# Revit family: T-604_Ciclon CC
name_source: partatom
category: Plumbing Fixtures
revit_build: Autodesk Revit 2015 (Build: 20140606_1530(x64)
units: mm (PartAtom-declared; Revit-internal decimal feet)

## types (3) — shared parameters
Altura máx. de bombeo = 6 m vertical
Amax = 200 mm  [stored 0.656168 ft]
Amin = 75 mm
Anchura = 500 mm  [stored 1.64042 ft]
Bastidor_Material principal = Jimten_Bastidor Azul
Bastidor_Material secundario = Jimten_Bastidor Acero
Carga aparente = 200 VA
Caudal = 1.7 L/s
Certificados = http://www.jimten.com
"
Cisterna = Jimten_Cisterna
Clasificación de cargas = Aparato eléctrico - Unidad de vivienda
Description = CISTERNA EMPOTRADA CON TRITURADOR SANITARIO PARA CUARTO DE BAÑO
Diámetro Cisterna = 40 mm  [stored 0.131234 ft]
Diámetro Impulsión = 32 mm  [stored 0.104987 ft]
Diámetro Toma Dcha = 40 mm  [stored 0.131234 ft]
Diámetro Toma Izq = 40 mm  [stored 0.131234 ft]
Diámetro Toma Superior = 40 mm  [stored 0.131234 ft]
Diámetro WC = 80 mm  [stored 0.262467 ft]
Electricidad = 220-240 VAC 50HZ
Electrodomésticos = No
Entradas = 3 x Ø40 mm
Fondo max = 220 mm  [stored 0.721785 ft]
Fondo min = 177 mm
Manufacturer = Jimten
Model = T-604CC CICLON CC
Número de polos = 1
Potencia = 470 W
Salida = 1 x Ø32mm
Triturador sanitario = Jimten_Triturador
Type Comments = FACIL MANTENIMIENTO GRACIAS A SU SISTEMA CASET. SILENCIOSO.
URL = http://www.jimten.com
"
Ud.Desagüe Bidé-Ducha = 2
Ud.Desagüe Lavabo = 1
Voltaje = 230 V
WC = Yes
WFU = 2
zero-valued in all types: Cost

## per-type parameters (varying)
| type | MaterialPanel | Panel | Referencia |
| T-604 CC Blanco | Jimten_Panel Blanco | Yes | 75902 |
| T-604 CC Negro | Jimten_Panel Negro | Yes | 75903 |
| T-604 CC | Jimten_Bastidor Acero | No | 75901 |

note: [stored X ft] marks values corroborated as IEEE doubles in the binary element streams (Revit-internal decimal feet)

## geometry (parser evidence)
native form markers: Blend x3, Sweep x8
no freeform markers — native parametric forms only
